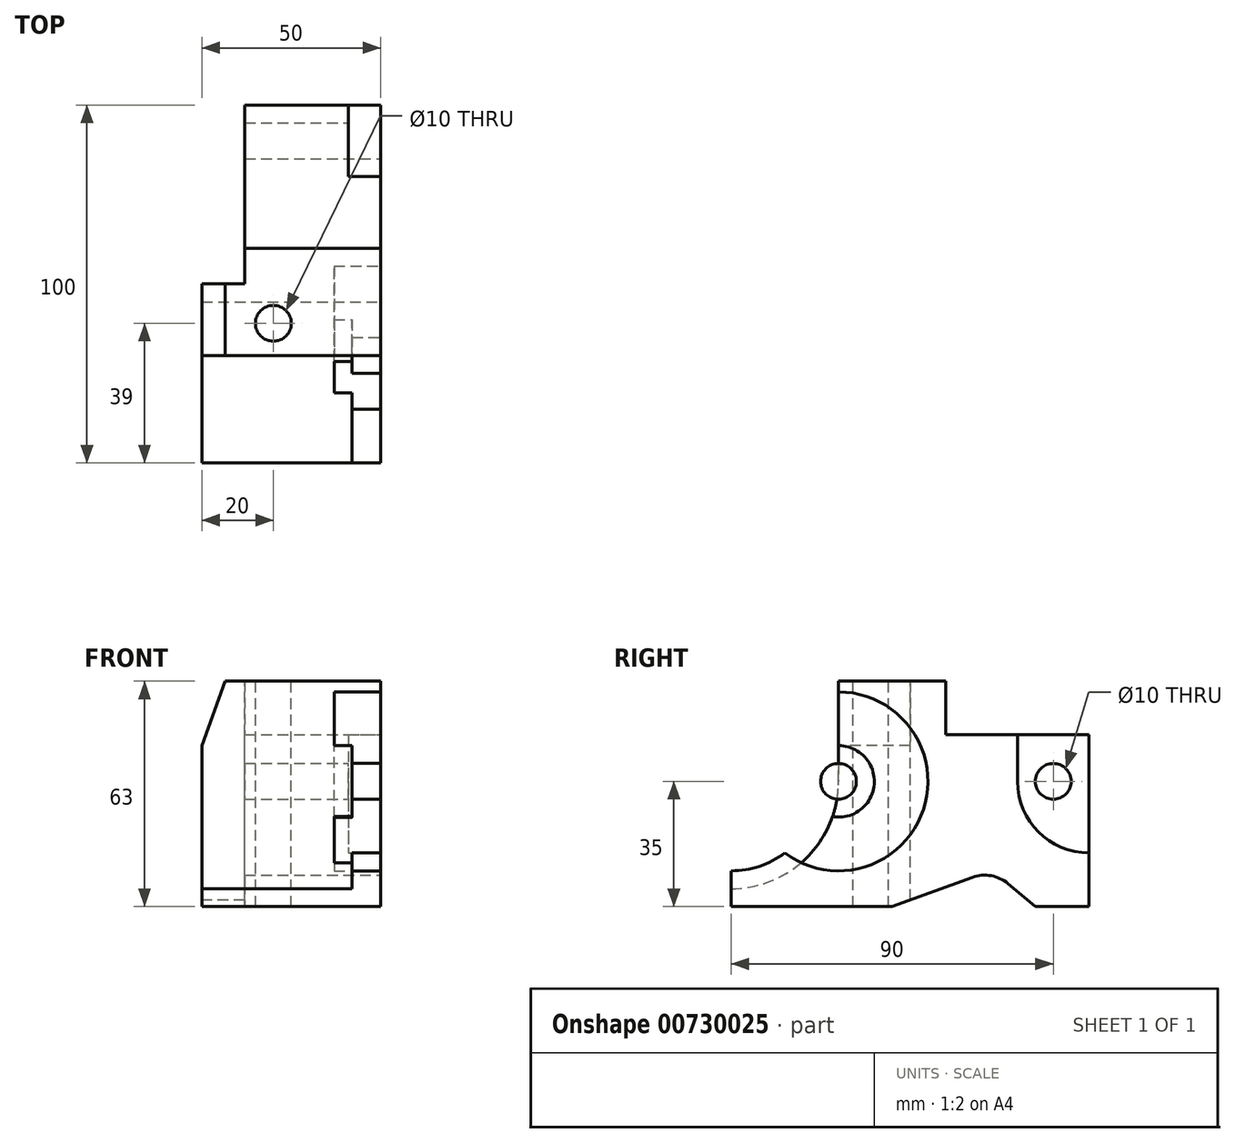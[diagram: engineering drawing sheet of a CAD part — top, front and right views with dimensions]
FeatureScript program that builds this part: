
annotation { "Feature Type Name" : "Feature", "Feature Type Description" : "" }
export const myFeature = defineFeature(function(context is Context, id is Id, definition is map)
    precondition{}
    {
        {
            var Q0;
            Q0=qCreatedBy(makeId("Top.planeOp"),FACE);
            var sketch = newSketch(context, id + "F0", { "sketchPlane" : qUnion([Q0])});
            skLineSegment(sketch, "E0.bottom", {"start": v(25, 50) * mm, "end": v(-25, 50) * mm});
            skLineSegment(sketch, "E0.top", {"start": v(25, -50) * mm, "end": v(-25, -50) * mm});
            skLineSegment(sketch, "E0.left", {"start": v(25, 50) * mm, "end": v(25, -50) * mm});
            skLineSegment(sketch, "E0.right", {"start": v(-25, 50) * mm, "end": v(-25, -50) * mm});
            skPoint(sketch, "E0.middle", {"position": v(0, 0) * mm});
            skSolve(sketch);
        }
        {
            var Q0;
            Q0 = qSketchRegion(id + "F0", true);
            extrude(context, id + "F1", {"entities" : qUnion([Q0]), "endBound" : BoundingType.SYMMETRIC, "depth" : 63 * mm, "offsetDistance" : 25.4 * mm});
        }
        {
            var Q0;
            Q0=makeQuery(id+"F1.opExtrude","SWEPT_FACE",FACE,{"disambiguationData":[OSD([sQuery(id+"F0.wireOp",EDGE,"E0.left")])]});
            var sketch = newSketch(context, id + "F2", { "sketchPlane" : qUnion([Q0])});
            skLineSegment(sketch, "E1", {"start": v(-5, -31.5) * mm, "end": v(17.47, -23.32) * mm});
            skLineSegment(sketch, "E2", {"start": v(27.32, -25.06) * mm, "end": v(35, -31.5) * mm});
            skPoint(sketch, "E3.visualSharp", {"position": v(22.9, -21.35) * mm});
            skArc(sketch, "E3.filletArc", {"start": v(27.32, -25.06) * mm, "mid": v(22.63, -22.87) * mm, "end": v(17.47, -23.32) * mm});
            skLineSegment(sketch, "E4.bottom", {"start": v(50, 31.5) * mm, "end": v(10, 31.5) * mm});
            skLineSegment(sketch, "E4.top", {"start": v(50, 16.5) * mm, "end": v(10, 16.5) * mm});
            skLineSegment(sketch, "E4.left", {"start": v(50, 31.5) * mm, "end": v(50, 16.5) * mm});
            skLineSegment(sketch, "E4.right", {"start": v(10, 31.5) * mm, "end": v(10, 16.5) * mm});
            skCircle(sketch, "E5", {"center": v(40, 3.5) * mm, "radius": 5 * mm});
            skSolve(sketch);
        }
        {
            var Q0;
            Q0 = qSketchRegion(id + "F2", true);
            var Q1;
            {var subQ0=sQuery(id+"F2.wireOp",EDGE,"E1");Q1=makeQuery(id+"F2.imprint","IMPRINT",FACE,{"disambiguationData":[TD([[makeQuery(id+"F2.imprint","IMPRINT",EDGE,{"derivedFrom":subQ0}),-1.0]])]});}
            extrude(context, id + "F3", {"entities" : qUnion([Q0, Q1]), "operationType" : NewBodyOperationType.REMOVE, "endBound" : BoundingType.THROUGH_ALL, "oppositeDirection" : true, "depth" : 25.4 * mm, "offsetDistance" : 25.4 * mm});
        }
        {
            var Q0;
            Q0=makeQuery(id+"F1.opExtrude","SWEPT_FACE",FACE,{"disambiguationData":[OSD([sQuery(id+"F0.wireOp",EDGE,"E0.left")])]});
            var sketch = newSketch(context, id + "F4", { "sketchPlane" : qUnion([Q0])});
            skLineSegment(sketch, "E6", {"start": v(30, 16.5) * mm, "end": v(30, 3.5) * mm});
            skArc(sketch, "E7", {"start": v(30, 3.5) * mm, "mid": v(35.86, -10.64) * mm, "end": v(50, -16.5) * mm});
            skSolve(sketch);
        }
        {
            var Q0;
            Q0 = qSketchRegion(id + "F4", true);
            var Q1;
            {var subQ3=sQuery(id+"F4.wireOp",EDGE,"E6");Q1=makeQuery(id+"F4.imprint","IMPRINT",FACE,{"disambiguationData":[TD([[makeQuery(id+"F4.imprint","IMPRINT",EDGE,{"derivedFrom":subQ3}),1.0]])]});}
            extrude(context, id + "F5", {"entities" : qUnion([Q0, Q1]), "operationType" : NewBodyOperationType.REMOVE, "oppositeDirection" : true, "depth" : 9 * mm, "offsetDistance" : 25.4 * mm});
        }
        {
            var Q0;
            Q0=makeQuery(id+"F1.opExtrude","SWEPT_FACE",FACE,{"disambiguationData":[OSD([sQuery(id+"F0.wireOp",EDGE,"E0.left")])]});
            var sketch = newSketch(context, id + "F6", { "sketchPlane" : qUnion([Q0])});
            skCircle(sketch, "E8", {"center": v(-20, 3.5) * mm, "radius": 5 * mm});
            skCircle(sketch, "E9", {"center": v(-20, 3.5) * mm, "radius": 10 * mm});
            skSolve(sketch);
        }
        {
            var Q0;
            Q0=makeQuery(id+"F6.imprint","IMPRINT",FACE,{"disambiguationData":[TD([[makeQuery(id+"F6.imprint","IMPRINT",EDGE,{"derivedFrom":sQuery(id+"F6.wireOp",EDGE,"E8")}),-1.0]])]});
            extrude(context, id + "F7", {"entities" : qUnion([Q0]), "operationType" : NewBodyOperationType.REMOVE, "oppositeDirection" : true, "depth" : 8 * mm, "offsetDistance" : 25.4 * mm});
        }
        {
            var Q0;
            Q0=makeQuery(id+"F7.boolean.opBoolean","SPLIT",FACE,{"disambiguationData":[TD([makeQuery(id+"F7.opExtrude","SWEPT_FACE",FACE,{"disambiguationData":[OSD([sQuery(id+"F6.wireOp",EDGE,"E8")])]})])],"derivedFrom":makeQuery(id+"F1.opExtrude","SWEPT_FACE",FACE,{"disambiguationData":[OSD([sQuery(id+"F0.wireOp",EDGE,"E0.left")])]})});
            var sketch = newSketch(context, id + "F8", { "sketchPlane" : qUnion([Q0])});
            skCircle(sketch, "E10", {"center": v(-20, 3.5) * mm, "radius": 25 * mm});
            skCircle(sketch, "E11.0", {"center": v(-20, 3.5) * mm, "radius": 10 * mm});
            skSolve(sketch);
        }
        {
            var Q0;
            Q0=makeQuery(id+"F8.imprint","IMPRINT",FACE,{"disambiguationData":[TD([[makeQuery(id+"F8.imprint","IMPRINT",EDGE,{"derivedFrom":sQuery(id+"F8.wireOp",EDGE,"E10")}),1.0]])]});
            extrude(context, id + "F9", {"entities" : qUnion([Q0]), "operationType" : NewBodyOperationType.REMOVE, "oppositeDirection" : true, "depth" : 13 * mm, "offsetDistance" : 25.4 * mm});
        }
        {
            var Q0;
            Q0=makeQuery(id+"F7.boolean.opBoolean","COPY",FACE,{"derivedFrom":makeQuery(id+"F7.opExtrude","CAP_FACE",FACE,{"disambiguationData":[OSD([sQuery(id+"F6.wireOp",EDGE,"E8"),sQuery(id+"F6.wireOp",EDGE,"E9")])],"isStart":false})});
            var sketch = newSketch(context, id + "F10", { "sketchPlane" : qUnion([Q0])});
            skCircle(sketch, "E12", {"center": v(-50, 3.5) * mm, "radius": 25 * mm});
            skLineSegment(sketch, "E13.0", {"start": v(-50, 31.5) * mm, "end": v(-50, -31.5) * mm, "construction": true});
            skSolve(sketch);
        }
        {
            var Q0;
            Q0 = qSketchRegion(id + "F10", true);
            extrude(context, id + "F11", {"entities" : qUnion([Q0]), "operationType" : NewBodyOperationType.REMOVE, "depth" : 25.4 * mm, "offsetDistance" : 25.4 * mm});
        }
        {
            var Q0;
            Q0=makeQuery(id+"F7.boolean.opBoolean","COPY",FACE,{"derivedFrom":makeQuery(id+"F7.opExtrude","CAP_FACE",FACE,{"disambiguationData":[OSD([sQuery(id+"F6.wireOp",EDGE,"E8"),sQuery(id+"F6.wireOp",EDGE,"E9")])],"isStart":false})});
            var sketch = newSketch(context, id + "F12", { "sketchPlane" : qUnion([Q0])});
            skCircle(sketch, "E14", {"center": v(-50, 3.5) * mm, "radius": 30 * mm});
            skArc(sketch, "E15.0", {"start": v(-50, 28.5) * mm, "mid": v(-42.1, 27.22) * mm, "end": v(-35, 23.5) * mm, "construction": true});
            skSolve(sketch);
        }
        {
            var Q0;
            Q0 = qSketchRegion(id + "F12", true);
            var Q1;
            Q1=makeQuery(id+"F1.opExtrude","SWEPT_FACE",FACE,{"disambiguationData":[OSD([sQuery(id+"F0.wireOp",EDGE,"E0.right")])]});
            extrude(context, id + "F13", {"entities" : qUnion([Q0]), "operationType" : NewBodyOperationType.REMOVE, "endBound" : BoundingType.UP_TO_SURFACE, "oppositeDirection" : true, "depth" : 25.4 * mm, "endBoundEntityFace" : qUnion([Q1]), "offsetDistance" : 25.4 * mm});
        }
        {
            var Q0;
            Q0=makeQuery(id+"F7.boolean.opBoolean","COPY",FACE,{"derivedFrom":makeQuery(id+"F7.opExtrude","CAP_FACE",FACE,{"disambiguationData":[OSD([sQuery(id+"F6.wireOp",EDGE,"E8"),sQuery(id+"F6.wireOp",EDGE,"E9")])],"isStart":false})});
            var sketch = newSketch(context, id + "F14", { "sketchPlane" : qUnion([Q0])});
            skLineSegment(sketch, "E16.0", {"start": v(-20, 31.5) * mm, "end": v(-50, 31.5) * mm});
            skLineSegment(sketch, "E17.0", {"start": v(-50, 31.5) * mm, "end": v(-50, 28.5) * mm});
            skLineSegment(sketch, "E18.bottom", {"start": v(-50, 31.5) * mm, "end": v(-20, 31.5) * mm});
            skLineSegment(sketch, "E18.top", {"start": v(-50, 3.5) * mm, "end": v(-20, 3.5) * mm});
            skLineSegment(sketch, "E18.left", {"start": v(-50, 31.5) * mm, "end": v(-50, 3.5) * mm});
            skLineSegment(sketch, "E18.right", {"start": v(-20, 31.5) * mm, "end": v(-20, 3.5) * mm});
            skPoint(sketch, "E19.orphan", {"position": v(10, 31.5) * mm});
            skSolve(sketch);
        }
        {
            var Q0;
            Q0 = qSketchRegion(id + "F14", true);
            var Q1;
            Q1=makeQuery(id+"F1.opExtrude","SWEPT_FACE",FACE,{"disambiguationData":[OSD([sQuery(id+"F0.wireOp",EDGE,"E0.right")])]});
            extrude(context, id + "F15", {"entities" : qUnion([Q0]), "operationType" : NewBodyOperationType.REMOVE, "endBound" : BoundingType.UP_TO_SURFACE, "oppositeDirection" : true, "depth" : 25.4 * mm, "endBoundEntityFace" : qUnion([Q1]), "offsetDistance" : 25.4 * mm});
        }
        {
            var Q0;
            {var subQ1=sQuery(id+"F12.wireOp",EDGE,"E14");Q0=makeQuery(id+"F15.boolean.opBoolean","MERGE",FACE,{"derivedFrom":[makeQuery(id+"F13.boolean.opBoolean","COPY",FACE,{"disambiguationData":[TD([makeQuery(id+"F11.boolean.opBoolean","COPY",FACE,{"disambiguationData":[OD(1.0)],"derivedFrom":makeQuery(id+"F11.opExtrude","SWEPT_FACE",FACE,{"disambiguationData":[OSD([sQuery(id+"F10.wireOp",EDGE,"E12")])]})})])],"derivedFrom":makeQuery(id+"F13.opExtrude","CAP_FACE",FACE,{"disambiguationData":[OSD([subQ1])],"isStart":true})}),makeQuery(id+"F15.opExtrude","CAP_FACE",FACE,{"disambiguationData":[OSD([sQuery(id+"F14.wireOp",EDGE,"E18.bottom"),sQuery(id+"F14.wireOp",EDGE,"E18.top"),sQuery(id+"F14.wireOp",EDGE,"E18.left"),sQuery(id+"F14.wireOp",EDGE,"E18.right")])],"isStart":true})]});}
            var sketch = newSketch(context, id + "F16", { "sketchPlane" : qUnion([Q0])});
            skLineSegment(sketch, "E20.bottom", {"start": v(20, 31.5) * mm, "end": v(54.71, 31.5) * mm});
            skLineSegment(sketch, "E20.top", {"start": v(20, 16.14) * mm, "end": v(54.71, 16.14) * mm});
            skLineSegment(sketch, "E20.left", {"start": v(20, 31.5) * mm, "end": v(20, 16.14) * mm});
            skLineSegment(sketch, "E20.right", {"start": v(54.71, 31.5) * mm, "end": v(54.71, 16.14) * mm});
            skSolve(sketch);
        }
        {
            var Q0;
            Q0 = qSketchRegion(id + "F16", true);
            extrude(context, id + "F17", {"entities" : qUnion([Q0]), "operationType" : NewBodyOperationType.REMOVE, "endBound" : BoundingType.THROUGH_ALL, "oppositeDirection" : true, "depth" : 25.4 * mm, "offsetDistance" : 25.4 * mm});
        }
        {
            var Q0;
            Q0=makeQuery(id+"F1.opExtrude","CAP_FACE",FACE,{"disambiguationData":[OSD([sQuery(id+"F0.wireOp",EDGE,"E0.bottom"),sQuery(id+"F0.wireOp",EDGE,"E0.top"),sQuery(id+"F0.wireOp",EDGE,"E0.left"),sQuery(id+"F0.wireOp",EDGE,"E0.right")])],"isStart":false});
            var sketch = newSketch(context, id + "F18", { "sketchPlane" : qUnion([Q0])});
            skCircle(sketch, "E21", {"center": v(-5, -11) * mm, "radius": 5 * mm});
            skLineSegment(sketch, "E22.0", {"start": v(-25, 50) * mm, "end": v(-13, 50) * mm});
            skLineSegment(sketch, "E23.0", {"start": v(-25, 50) * mm, "end": v(-25, 10) * mm});
            skLineSegment(sketch, "E24.top", {"start": v(-25, 0) * mm, "end": v(-13, 0) * mm});
            skLineSegment(sketch, "E24.left", {"start": v(-25, 50) * mm, "end": v(-25, 0) * mm});
            skLineSegment(sketch, "E24.right", {"start": v(-13, 50) * mm, "end": v(-13, 0) * mm});
            skPoint(sketch, "E25.orphan", {"position": v(16, 50) * mm});
            skSolve(sketch);
        }
        {
            var Q0;
            Q0 = qSketchRegion(id + "F18", true);
            extrude(context, id + "F19", {"entities" : qUnion([Q0]), "operationType" : NewBodyOperationType.REMOVE, "endBound" : BoundingType.THROUGH_ALL, "oppositeDirection" : true, "depth" : 25.4 * mm, "offsetDistance" : 25.4 * mm});
        }
        {
            var Q0;
            Q0=makeQuery(id+"F17.boolean.opBoolean","MERGE",FACE,{"derivedFrom":[makeQuery(id+"F15.boolean.opBoolean","COPY",FACE,{"derivedFrom":makeQuery(id+"F15.opExtrude","SWEPT_FACE",FACE,{"disambiguationData":[OSD([sQuery(id+"F14.wireOp",EDGE,"E18.right")])]})}),makeQuery(id+"F17.opExtrude","SWEPT_FACE",FACE,{"disambiguationData":[OSD([sQuery(id+"F16.wireOp",EDGE,"E20.left")])]})]});
            var sketch = newSketch(context, id + "F20", { "sketchPlane" : qUnion([Q0])});
            skLineSegment(sketch, "E26", {"start": v(-18.45, 31.5) * mm, "end": v(-25, 13.5) * mm});
            skLineSegment(sketch, "E27", {"start": v(-25, 13.5) * mm, "end": v(-25, 31.5) * mm});
            skLineSegment(sketch, "E28", {"start": v(-25, 31.5) * mm, "end": v(-18.45, 31.5) * mm});
            skSolve(sketch);
        }
        {
            var Q0;
            Q0 = qSketchRegion(id + "F20", true);
            extrude(context, id + "F21", {"entities" : qUnion([Q0]), "operationType" : NewBodyOperationType.REMOVE, "endBound" : BoundingType.THROUGH_ALL, "oppositeDirection" : true, "depth" : 25.4 * mm, "offsetDistance" : 25.4 * mm});
        }
    });
